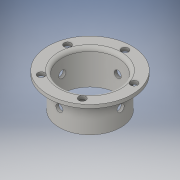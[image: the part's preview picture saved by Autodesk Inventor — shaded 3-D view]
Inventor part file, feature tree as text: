
AUTODESK INVENTOR PART (.ipt)
format: ipt  version: 2016 (Build 200138000, 138)  size: 589,312 bytes
history: native  units: in
note: dims shown in document units (in); Inventor stores cm internally (conversion verified against a paired STEP export)
features: sketch x6, extrude x3, hole x2, pattern_circular x2, projected_geometry x2, shell x1, fillet x1, plane x1
ambient origin geometry x8: Origin, YZ Plane, XZ Plane, XY Plane, X Axis, Y Axis, Z Axis, Center Point
bodies: Solid1 (feature_tree)
feature tree (18):
  extrude  "Extrusion1"  Depth=1.0in TaperAngle=0.0deg
  shell  "Shell1"  Thickness=0.1in
  extrude  "Extrusion2"  Depth=0.125in TaperAngle=0.0deg
  extrude  "Extrusion3"  Depth=2.5in
  hole  "Hole1"  [1 undecoded]
  pattern_circular  "Circular Pattern1"  Count=4 Angle=360.0deg
  fillet  "Fillet1"  [1 undecoded]
  plane  "Work Plane1"
  sketch  "Sketch5"  dims[d20=0.125in]
  hole  "Hole2"  [1 undecoded]
  pattern_circular  "Circular Pattern2"  [2 undecoded]
  sketch  "Sketch1"  dims[d0=2.0in d1=1.0in d2=0.0in d3=0.1in]
  sketch  "Sketch2"  dims[d4=3.0in d5=0.125in d6=0.0in]
  sketch  "Sketch3"  dims[d7=0.125in d8=0.0in d9=2.5in]
  projected_geometry  "Projected Loop1"
  sketch  "Sketch4"  dims[d10=0.255in d11=0.75in d12=0.375in d13=0.25in d14=0.5635in d15=1.0in d16=0.8108in d17=1.9685in d18=360.0deg]
  projected_geometry  "Projected Loop2"
  sketch  "Sketch6"  dims[d21=-0.625in d22=0.255in d23=0.75in d24=0.375in d25=0.25in d26=0.5635in d27=1.0in d28=0.8108in d29=1.5748in d30=360.0deg]
note: 5 required parameter values undecoded (feature->parameter linkage not recoverable at this tier; creation-order binding heuristic only, values carry confidence <= 0.55)
